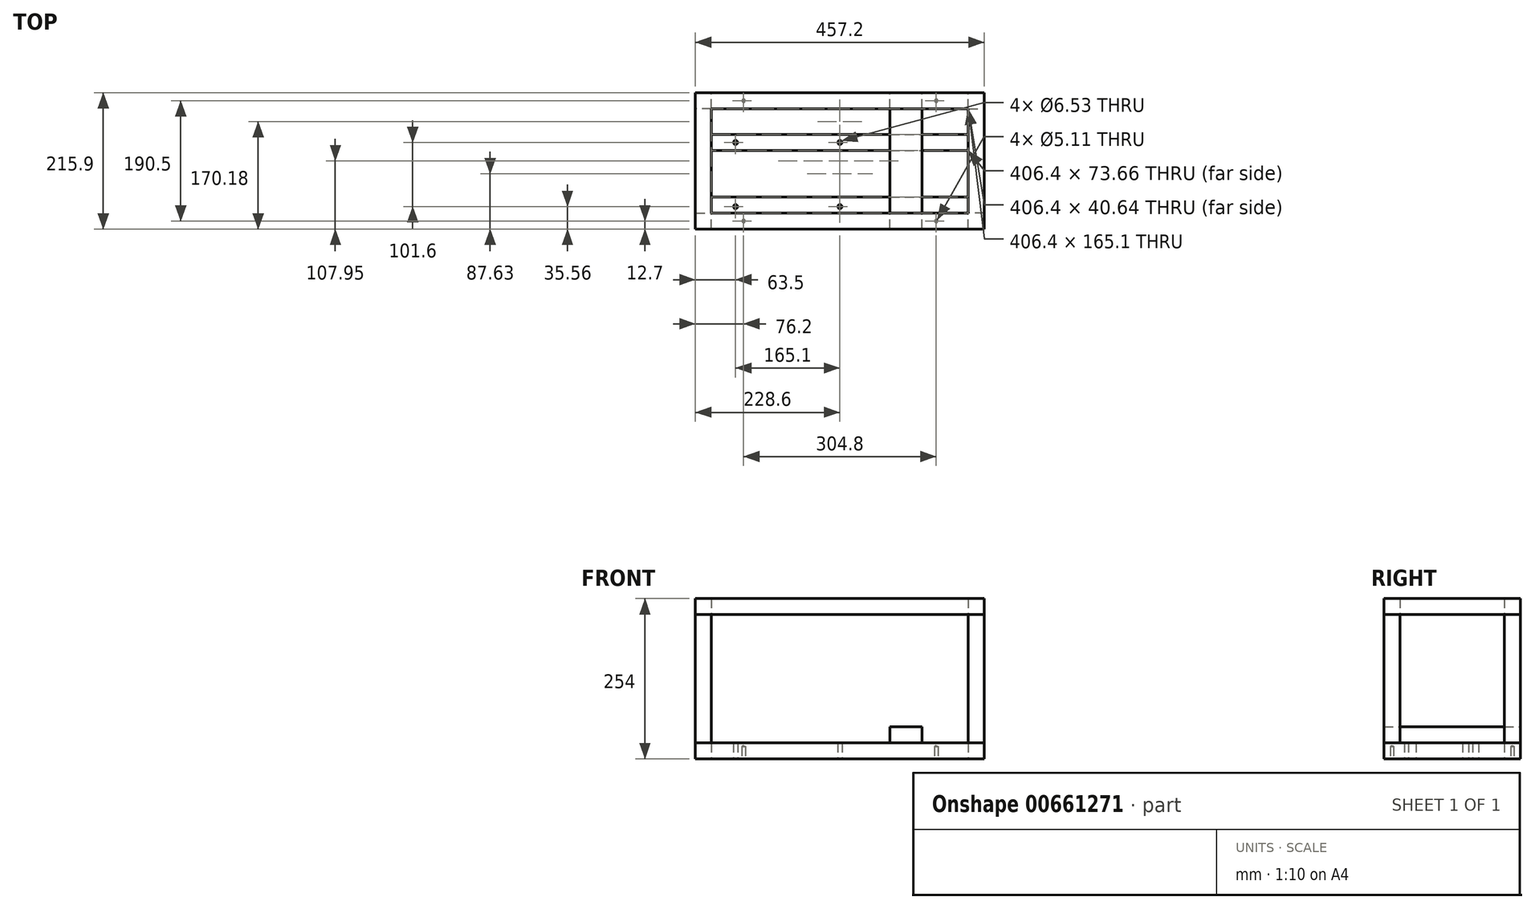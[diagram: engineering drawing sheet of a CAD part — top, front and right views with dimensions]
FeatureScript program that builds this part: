
annotation { "Feature Type Name" : "Feature", "Feature Type Description" : "" }
export const myFeature = defineFeature(function(context is Context, id is Id, definition is map)
    precondition{}
    {
        {
            var Q0;
            Q0=qCreatedBy(makeId("Top.planeOp"),FACE);
            var sketch = newSketch(context, id + "F0", { "sketchPlane" : qUnion([Q0])});
            skLineSegment(sketch, "E0.bottom", {"start": v(41.27, 172.72) * mm, "end": v(250.83, 172.72) * mm, "construction": true});
            skLineSegment(sketch, "E0.top", {"start": v(41.27, 0) * mm, "end": v(250.83, 0) * mm, "construction": true});
            skLineSegment(sketch, "E0.left", {"start": v(41.27, 172.72) * mm, "end": v(41.27, 0) * mm, "construction": true});
            skLineSegment(sketch, "E0.right", {"start": v(250.83, 172.72) * mm, "end": v(250.83, 0) * mm, "construction": true});
            skLineSegment(sketch, "E1.bottom", {"start": v(63.5, 137.16) * mm, "end": v(228.6, 137.16) * mm, "construction": true});
            skLineSegment(sketch, "E1.top", {"start": v(63.5, 35.56) * mm, "end": v(228.6, 35.56) * mm, "construction": true});
            skLineSegment(sketch, "E1.left", {"start": v(63.5, 137.16) * mm, "end": v(63.5, 35.56) * mm, "construction": true});
            skLineSegment(sketch, "E1.right", {"start": v(228.6, 137.16) * mm, "end": v(228.6, 35.56) * mm, "construction": true});
            skLineSegment(sketch, "E2", {"start": v(146.05, 172.72) * mm, "end": v(146.05, 137.16) * mm, "construction": true});
            skLineSegment(sketch, "E3", {"start": v(146.05, 35.56) * mm, "end": v(146.05, 0) * mm, "construction": true});
            skLineSegment(sketch, "E4", {"start": v(63.5, 86.36) * mm, "end": v(41.28, 86.36) * mm, "construction": true});
            skLineSegment(sketch, "E5", {"start": v(228.6, 86.36) * mm, "end": v(250.83, 86.36) * mm, "construction": true});
            skSolve(sketch);
        }
        {
            var Q0;
            Q0=qCreatedBy(makeId("Top.planeOp"),FACE);
            var sketch = newSketch(context, id + "F1", { "sketchPlane" : qUnion([Q0])});
            skLineSegment(sketch, "E6.bottom", {"start": v(0, 0) * mm, "end": v(457.2, 0) * mm});
            skLineSegment(sketch, "E6.top", {"start": v(0, 215.9) * mm, "end": v(457.2, 215.9) * mm});
            skLineSegment(sketch, "E6.left", {"start": v(0, 0) * mm, "end": v(0, 215.9) * mm});
            skLineSegment(sketch, "E6.right", {"start": v(457.2, 0) * mm, "end": v(457.2, 215.9) * mm});
            skLineSegment(sketch, "E7.bottom", {"start": v(25.4, 50.8) * mm, "end": v(431.8, 50.8) * mm});
            skLineSegment(sketch, "E7.top", {"start": v(25.4, 190.5) * mm, "end": v(431.8, 190.5) * mm});
            skLineSegment(sketch, "E7.left", {"start": v(25.4, 50.8) * mm, "end": v(25.4, 124.46) * mm});
            skLineSegment(sketch, "E7.right", {"start": v(431.8, 50.8) * mm, "end": v(431.8, 124.46) * mm});
            skLineSegment(sketch, "E8.bottom", {"start": v(25.4, 149.86) * mm, "end": v(431.8, 149.86) * mm});
            skLineSegment(sketch, "E8.top", {"start": v(25.4, 124.46) * mm, "end": v(431.8, 124.46) * mm});
            skLineSegment(sketch, "E9", {"start": v(63.5, 149.86) * mm, "end": v(63.5, 124.46) * mm, "construction": true});
            skLineSegment(sketch, "E10.trimOffspring", {"start": v(25.4, 149.86) * mm, "end": v(25.4, 190.5) * mm});
            skLineSegment(sketch, "E11.trimOffspring", {"start": v(431.8, 149.86) * mm, "end": v(431.8, 190.5) * mm});
            skSolve(sketch);
        }
        {
            var Q0;
            Q0=makeQuery(id+"F1.imprint","IMPRINT",FACE,{"disambiguationData":[TD([[makeQuery(id+"F1.imprint","IMPRINT",EDGE,{"derivedFrom":sQuery(id+"F1.wireOp",EDGE,"E6.bottom")}),1.0]])]});
            extrude(context, id + "F2", {"entities" : qUnion([Q0]), "depth" : 25.4 * mm, "offsetDistance" : 25.4 * mm});
        }
        {
            var Q0;
            Q0=sQuery(id+"F0.wireOp",VERTEX,"E1.top.start");
            var Q1;
            Q1=sQuery(id+"F0.wireOp",VERTEX,"E1.top.end");
            var Q2;
            Q2=makeQuery(id+"F2.opExtrude","SWEPT_BODY",BODY,{"disambiguationData":[OSD([sQuery(id+"F1.wireOp",EDGE,"E6.bottom"),sQuery(id+"F1.wireOp",EDGE,"E6.top"),sQuery(id+"F1.wireOp",EDGE,"E6.left"),sQuery(id+"F1.wireOp",EDGE,"E6.right"),sQuery(id+"F1.wireOp",EDGE,"E7.bottom"),sQuery(id+"F1.wireOp",EDGE,"E7.top"),sQuery(id+"F1.wireOp",EDGE,"E7.left"),sQuery(id+"F1.wireOp",EDGE,"E7.right")])]});
            hole(context, id + "F3", {"style" : HoleStyle.SIMPLE, "endStyle" : HoleEndStyle.THROUGH, "oppositeDirection" : true, "standardTappedOrClearance" : lookupTablePath({ "standard" : "ANSI", "engagement" : "75%", "pitch" : "18 tpi", "size" : "5/16", "type" : "Tapped" }), "standardBlindInLast" : lookupTablePath({ "standard" : "ANSI", "engagement" : "75%", "pitch" : "18 tpi", "size" : "5/16", "type" : "Tapped" }), "holeDiameter" : 6.53 * mm, "majorDiameter" : 7.94 * mm, "showTappedDepth" : true, "tappedDepth" : 18.41 * mm, "tapClearance" : 1, "startFromSketch" : true, "locations" : qUnion([Q0, Q1]), "scope" : qUnion([Q2])});
        }
        {
            var Q0;
            Q0=sQuery(id+"F0.wireOp",VERTEX,"E1.left.start");
            var Q1;
            Q1=sQuery(id+"F0.wireOp",VERTEX,"E1.bottom.end");
            var Q2;
            Q2=makeQuery(id+"F2.opExtrude","SWEPT_BODY",BODY,{"disambiguationData":[OSD([sQuery(id+"F1.wireOp",EDGE,"E6.bottom"),sQuery(id+"F1.wireOp",EDGE,"E6.top"),sQuery(id+"F1.wireOp",EDGE,"E6.left"),sQuery(id+"F1.wireOp",EDGE,"E6.right"),sQuery(id+"F1.wireOp",EDGE,"E7.bottom"),sQuery(id+"F1.wireOp",EDGE,"E7.top"),sQuery(id+"F1.wireOp",EDGE,"E7.left"),sQuery(id+"F1.wireOp",EDGE,"E7.right"),sQuery(id+"F1.wireOp",EDGE,"E8.bottom"),sQuery(id+"F1.wireOp",EDGE,"E8.top"),sQuery(id+"F1.wireOp",EDGE,"E10.trimOffspring"),sQuery(id+"F1.wireOp",EDGE,"E11.trimOffspring")])]});
            hole(context, id + "F4", {"style" : HoleStyle.SIMPLE, "endStyle" : HoleEndStyle.THROUGH, "oppositeDirection" : true, "standardTappedOrClearance" : lookupTablePath({ "standard" : "ANSI", "engagement" : "75%", "pitch" : "18 tpi", "size" : "5/16", "type" : "Tapped" }), "standardBlindInLast" : lookupTablePath({ "standard" : "ANSI", "engagement" : "75%", "pitch" : "18 tpi", "size" : "5/16", "type" : "Tapped" }), "holeDiameter" : 6.53 * mm, "majorDiameter" : 7.94 * mm, "showTappedDepth" : true, "tappedDepth" : 18.43 * mm, "tapClearance" : 1, "locations" : qUnion([Q0, Q1]), "scope" : qUnion([Q2])});
        }
        {
            var Q0;
            Q0=makeQuery(id+"F2.opExtrude","CAP_FACE",FACE,{"disambiguationData":[OSD([sQuery(id+"F1.wireOp",EDGE,"E6.bottom"),sQuery(id+"F1.wireOp",EDGE,"E6.top"),sQuery(id+"F1.wireOp",EDGE,"E6.left"),sQuery(id+"F1.wireOp",EDGE,"E6.right"),sQuery(id+"F1.wireOp",EDGE,"E7.bottom"),sQuery(id+"F1.wireOp",EDGE,"E7.top"),sQuery(id+"F1.wireOp",EDGE,"E7.left"),sQuery(id+"F1.wireOp",EDGE,"E7.right")])],"isStart":false});
            var sketch = newSketch(context, id + "F5", { "sketchPlane" : qUnion([Q0])});
            skLineSegment(sketch, "E12.bottom", {"start": v(307.98, 0) * mm, "end": v(358.78, 0) * mm});
            skLineSegment(sketch, "E12.top", {"start": v(307.98, 215.9) * mm, "end": v(358.78, 215.9) * mm});
            skLineSegment(sketch, "E12.left", {"start": v(307.98, 0) * mm, "end": v(307.98, 215.9) * mm});
            skLineSegment(sketch, "E12.right", {"start": v(358.78, 0) * mm, "end": v(358.78, 215.9) * mm});
            skSolve(sketch);
        }
        {
            var Q0;
            Q0 = qSketchRegion(id + "F5", true);
            extrude(context, id + "F6", {"entities" : qUnion([Q0]), "depth" : 25.4 * mm, "offsetDistance" : 25.4 * mm});
        }
        {
            var Q0;
            Q0=makeQuery(id+"F2.opExtrude","CAP_FACE",FACE,{"disambiguationData":[OSD([sQuery(id+"F1.wireOp",EDGE,"E6.bottom"),sQuery(id+"F1.wireOp",EDGE,"E6.top"),sQuery(id+"F1.wireOp",EDGE,"E6.left"),sQuery(id+"F1.wireOp",EDGE,"E6.right"),sQuery(id+"F1.wireOp",EDGE,"E7.bottom"),sQuery(id+"F1.wireOp",EDGE,"E7.top"),sQuery(id+"F1.wireOp",EDGE,"E7.left"),sQuery(id+"F1.wireOp",EDGE,"E7.right")])],"isStart":false});
            var sketch = newSketch(context, id + "F7", { "sketchPlane" : qUnion([Q0])});
            skLineSegment(sketch, "E13.bottom", {"start": v(25.4, 190.5) * mm, "end": v(0, 190.5) * mm});
            skLineSegment(sketch, "E13.top", {"start": v(25.4, 215.9) * mm, "end": v(0, 215.9) * mm});
            skLineSegment(sketch, "E13.left", {"start": v(25.4, 190.5) * mm, "end": v(25.4, 215.9) * mm});
            skLineSegment(sketch, "E13.right", {"start": v(0, 190.5) * mm, "end": v(0, 215.9) * mm});
            skLineSegment(sketch, "E14.bottom", {"start": v(431.8, 190.5) * mm, "end": v(457.2, 190.5) * mm});
            skLineSegment(sketch, "E14.top", {"start": v(431.8, 215.9) * mm, "end": v(457.2, 215.9) * mm});
            skLineSegment(sketch, "E14.left", {"start": v(431.8, 190.5) * mm, "end": v(431.8, 215.9) * mm});
            skLineSegment(sketch, "E14.right", {"start": v(457.2, 190.5) * mm, "end": v(457.2, 215.9) * mm});
            skLineSegment(sketch, "E15.bottom", {"start": v(457.2, 0) * mm, "end": v(431.8, 0) * mm});
            skLineSegment(sketch, "E15.top", {"start": v(457.2, 25.4) * mm, "end": v(431.8, 25.4) * mm});
            skLineSegment(sketch, "E15.left", {"start": v(457.2, 0) * mm, "end": v(457.2, 25.4) * mm});
            skLineSegment(sketch, "E15.right", {"start": v(431.8, 0) * mm, "end": v(431.8, 25.4) * mm});
            skLineSegment(sketch, "E16.bottom", {"start": v(-14.83, 0) * mm, "end": v(25.4, 0) * mm});
            skLineSegment(sketch, "E16.top", {"start": v(0, 25.4) * mm, "end": v(25.4, 25.4) * mm});
            skLineSegment(sketch, "E16.left", {"start": v(0, 0) * mm, "end": v(0, 25.4) * mm});
            skLineSegment(sketch, "E16.right", {"start": v(25.4, 0) * mm, "end": v(25.4, 25.4) * mm});
            skSolve(sketch);
        }
        {
            var Q0;
            Q0 = qSketchRegion(id + "F7", true);
            extrude(context, id + "F8", {"entities" : qUnion([Q0]), "depth" : 203.2 * mm, "offsetDistance" : 25.4 * mm});
        }
        {
            var Q0;
            Q0=makeQuery(id+"F8.opExtrude","CAP_FACE",FACE,{"disambiguationData":[OSD([sQuery(id+"F7.wireOp",EDGE,"E16.bottom"),sQuery(id+"F7.wireOp",EDGE,"E16.top"),sQuery(id+"F7.wireOp",EDGE,"E16.left"),sQuery(id+"F7.wireOp",EDGE,"E16.right")])],"isStart":false});
            var sketch = newSketch(context, id + "F9", { "sketchPlane" : qUnion([Q0])});
            skLineSegment(sketch, "E17.bottom", {"start": v(0, 215.9) * mm, "end": v(457.2, 215.9) * mm});
            skLineSegment(sketch, "E17.top", {"start": v(0, 0) * mm, "end": v(457.2, 0) * mm});
            skLineSegment(sketch, "E17.left", {"start": v(0, 215.9) * mm, "end": v(0, 0) * mm});
            skLineSegment(sketch, "E17.right", {"start": v(457.2, 215.9) * mm, "end": v(457.2, 0) * mm});
            skLineSegment(sketch, "E18.bottom", {"start": v(431.8, 25.4) * mm, "end": v(25.4, 25.4) * mm});
            skLineSegment(sketch, "E18.top", {"start": v(431.8, 190.5) * mm, "end": v(25.4, 190.5) * mm});
            skLineSegment(sketch, "E18.left", {"start": v(431.8, 25.4) * mm, "end": v(431.8, 190.5) * mm});
            skLineSegment(sketch, "E18.right", {"start": v(25.4, 25.4) * mm, "end": v(25.4, 190.5) * mm});
            skSolve(sketch);
        }
        {
            var Q0;
            Q0 = qSketchRegion(id + "F9", true);
            extrude(context, id + "F10", {"entities" : qUnion([Q0]), "depth" : 25.4 * mm, "offsetDistance" : 25.4 * mm});
        }
        {
            var Q0;
            Q0=makeQuery(id+"F2.opExtrude","CAP_FACE",FACE,{"disambiguationData":[OSD([sQuery(id+"F1.wireOp",EDGE,"E6.bottom"),sQuery(id+"F1.wireOp",EDGE,"E6.top"),sQuery(id+"F1.wireOp",EDGE,"E6.left"),sQuery(id+"F1.wireOp",EDGE,"E6.right"),sQuery(id+"F1.wireOp",EDGE,"E7.bottom"),sQuery(id+"F1.wireOp",EDGE,"E7.top"),sQuery(id+"F1.wireOp",EDGE,"E7.left"),sQuery(id+"F1.wireOp",EDGE,"E7.right")])],"isStart":true});
            var sketch = newSketch(context, id + "F11", { "sketchPlane" : qUnion([Q0])});
            skLineSegment(sketch, "E19.bottom", {"start": v(76.2, -203.2) * mm, "end": v(381, -203.2) * mm, "construction": true});
            skLineSegment(sketch, "E19.top", {"start": v(76.2, -12.7) * mm, "end": v(381, -12.7) * mm, "construction": true});
            skLineSegment(sketch, "E19.left", {"start": v(76.2, -203.2) * mm, "end": v(76.2, -12.7) * mm, "construction": true});
            skLineSegment(sketch, "E19.right", {"start": v(381, -203.2) * mm, "end": v(381, -12.7) * mm, "construction": true});
            skSolve(sketch);
        }
        {
            var Q0;
            Q0=sQuery(id+"F11.wireOp",VERTEX,"E19.bottom.end");
            var Q1;
            Q1=sQuery(id+"F11.wireOp",VERTEX,"E19.left.start");
            var Q2;
            Q2=sQuery(id+"F11.wireOp",VERTEX,"E19.top.start");
            var Q3;
            Q3=sQuery(id+"F11.wireOp",VERTEX,"E19.right.end");
            var Q4;
            Q4=makeQuery(id+"F2.opExtrude","SWEPT_BODY",BODY,{"disambiguationData":[OSD([sQuery(id+"F1.wireOp",EDGE,"E6.bottom"),sQuery(id+"F1.wireOp",EDGE,"E6.top"),sQuery(id+"F1.wireOp",EDGE,"E6.left"),sQuery(id+"F1.wireOp",EDGE,"E6.right"),sQuery(id+"F1.wireOp",EDGE,"E7.bottom"),sQuery(id+"F1.wireOp",EDGE,"E7.top"),sQuery(id+"F1.wireOp",EDGE,"E7.left"),sQuery(id+"F1.wireOp",EDGE,"E7.right")])]});
            hole(context, id + "F12", {"style" : HoleStyle.SIMPLE, "endStyle" : HoleEndStyle.BLIND, "standardTappedOrClearance" : lookupTablePath({ "standard" : "ANSI", "engagement" : "75%", "pitch" : "20 tpi", "size" : "1/4", "type" : "Tapped" }), "standardBlindInLast" : lookupTablePath({ "standard" : "ANSI", "engagement" : "75%", "pitch" : "20 tpi", "size" : "1/4", "type" : "Tapped" }), "holeDiameter" : 5.1 * mm, "majorDiameter" : 6.35 * mm, "showTappedDepth" : true, "holeDepth" : 19.68 * mm, "tappedDepth" : 18.41 * mm, "tapClearance" : 1, "locations" : qUnion([Q0, Q1, Q2, Q3]), "scope" : qUnion([Q4])});
        }
    });
